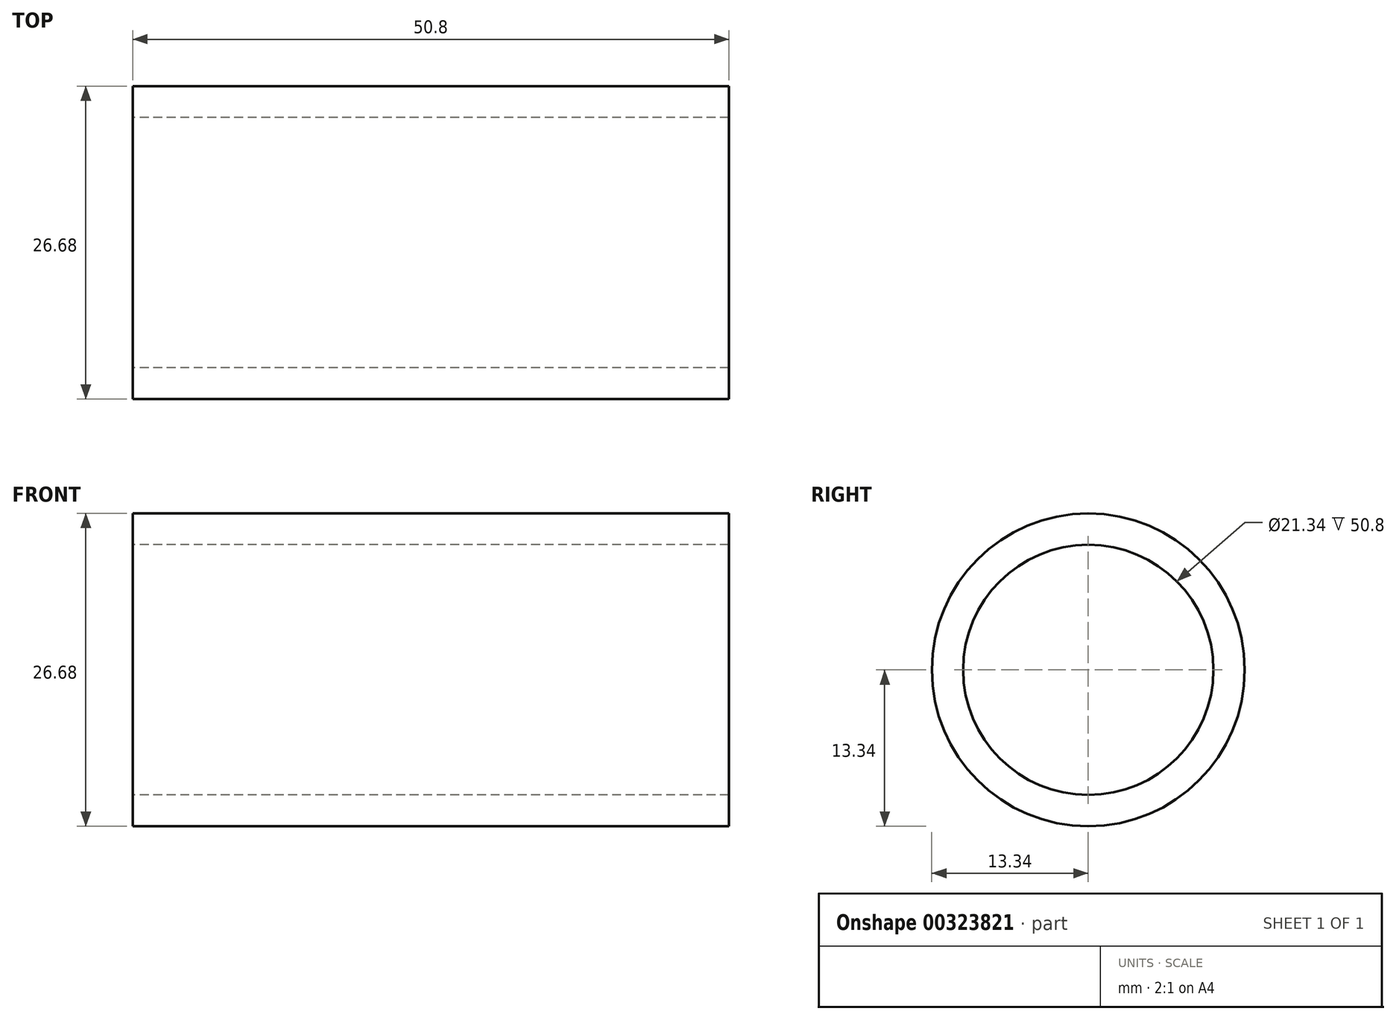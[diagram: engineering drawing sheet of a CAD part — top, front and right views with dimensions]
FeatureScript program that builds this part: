
annotation { "Feature Type Name" : "Feature", "Feature Type Description" : "" }
export const myFeature = defineFeature(function(context is Context, id is Id, definition is map)
    precondition{}
    {
        {
            var Q0;
            Q0=qCreatedBy(makeId("Right.planeOp"),FACE);
            var sketch = newSketch(context, id + "F0", { "sketchPlane" : qUnion([Q0])});
            skCircle(sketch, "E0", {"center": v(0, 0) * mm, "radius": 10.67 * mm});
            skCircle(sketch, "E1", {"center": v(0, 0) * mm, "radius": 13.33 * mm});
            skSolve(sketch);
        }
        {
            var Q0;
            Q0=makeQuery(id+"F0.imprint","IMPRINT",FACE,{"disambiguationData":[TD([[makeQuery(id+"F0.imprint","IMPRINT",EDGE,{"derivedFrom":sQuery(id+"F0.wireOp",EDGE,"E0")}),-1.0]])]});
            extrude(context, id + "F1", {"entities" : qUnion([Q0]), "depth" : 50.8 * mm});
        }
    });
